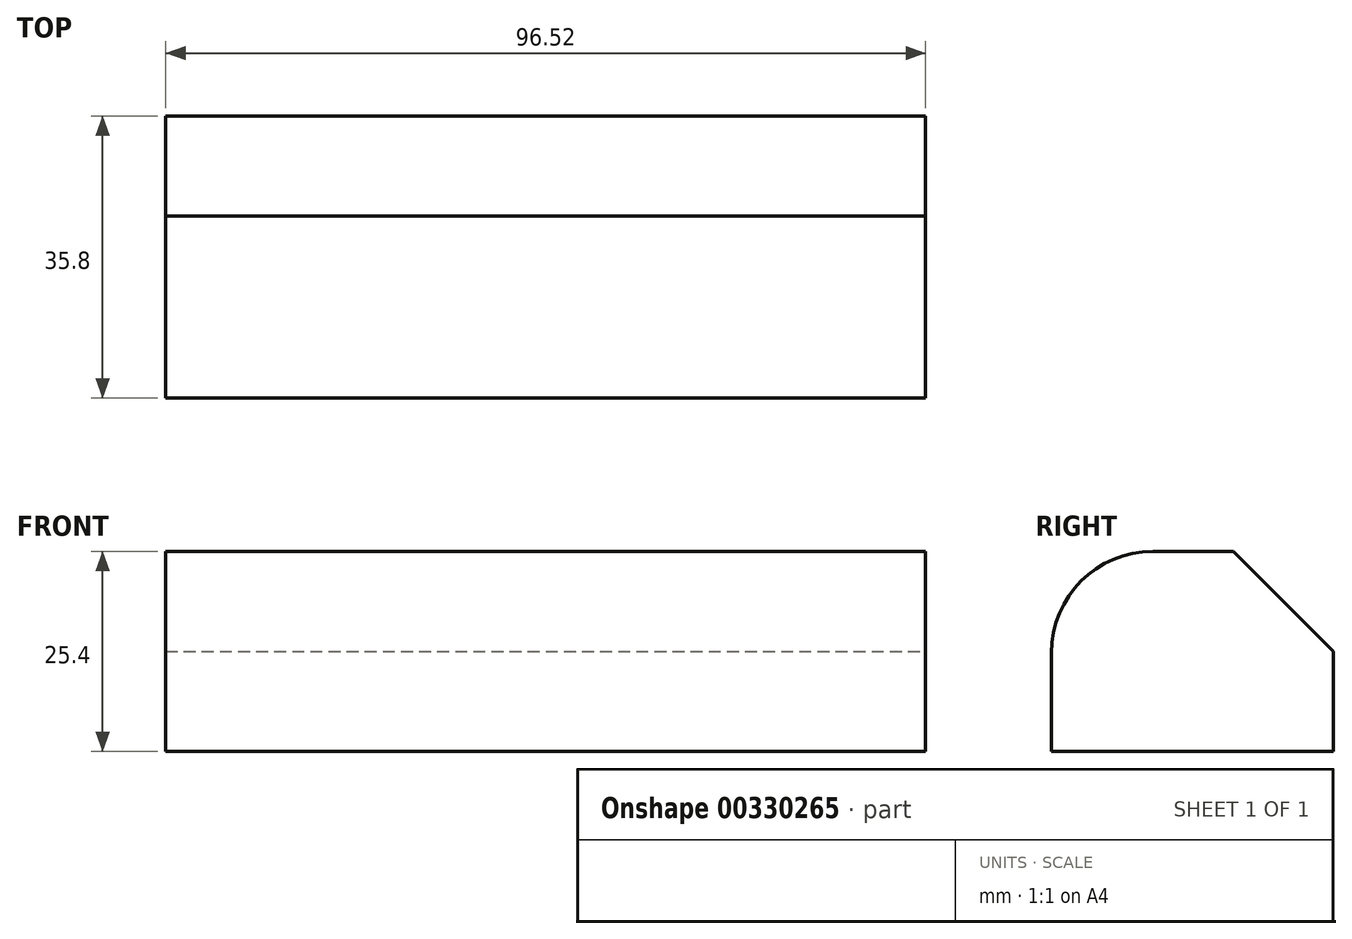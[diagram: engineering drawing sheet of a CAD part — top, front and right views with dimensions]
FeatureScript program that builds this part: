
annotation { "Feature Type Name" : "Feature", "Feature Type Description" : "" }
export const myFeature = defineFeature(function(context is Context, id is Id, definition is map)
    precondition{}
    {
        {
            var Q0;
            Q0=qCreatedBy(makeId("Top.planeOp"),FACE);
            var sketch = newSketch(context, id + "F0", { "sketchPlane" : qUnion([Q0])});
            skLineSegment(sketch, "E0.bottom", {"start": v(-61.35, 0) * mm, "end": v(35.17, 0) * mm});
            skLineSegment(sketch, "E0.top", {"start": v(-61.35, -35.8) * mm, "end": v(35.17, -35.8) * mm});
            skLineSegment(sketch, "E0.left", {"start": v(-61.35, 0) * mm, "end": v(-61.35, -35.8) * mm});
            skLineSegment(sketch, "E0.right", {"start": v(35.17, 0) * mm, "end": v(35.17, -35.8) * mm});
            skSolve(sketch);
        }
        {
            var Q0;
            Q0 = qSketchRegion(id + "F0", true);
            extrude(context, id + "F1", {"entities" : qUnion([Q0]), "depth" : 25.4 * mm});
        }
        {
            var Q0;
            Q0=makeQuery(id+"F1.opExtrude","CAP_EDGE",EDGE,{"disambiguationData":[OSD([sQuery(id+"F0.wireOp",EDGE,"E0.top")])],"isStart":false});
            fillet(context, id + "F2", {"entities" : qUnion([Q0]), "radius" : 12.88 * mm, "tangentPropagation" : true, "allowEdgeOverflow" : false});
        }
        {
            var Q0;
            Q0=makeQuery(id+"F1.opExtrude","CAP_EDGE",EDGE,{"disambiguationData":[OSD([sQuery(id+"F0.wireOp",EDGE,"E0.bottom")])],"isStart":false});
            chamfer(context, id + "F3", {"entities" : qUnion([Q0]), "width" : 12.7 * mm, "tangentPropagation" : true});
        }
    });
